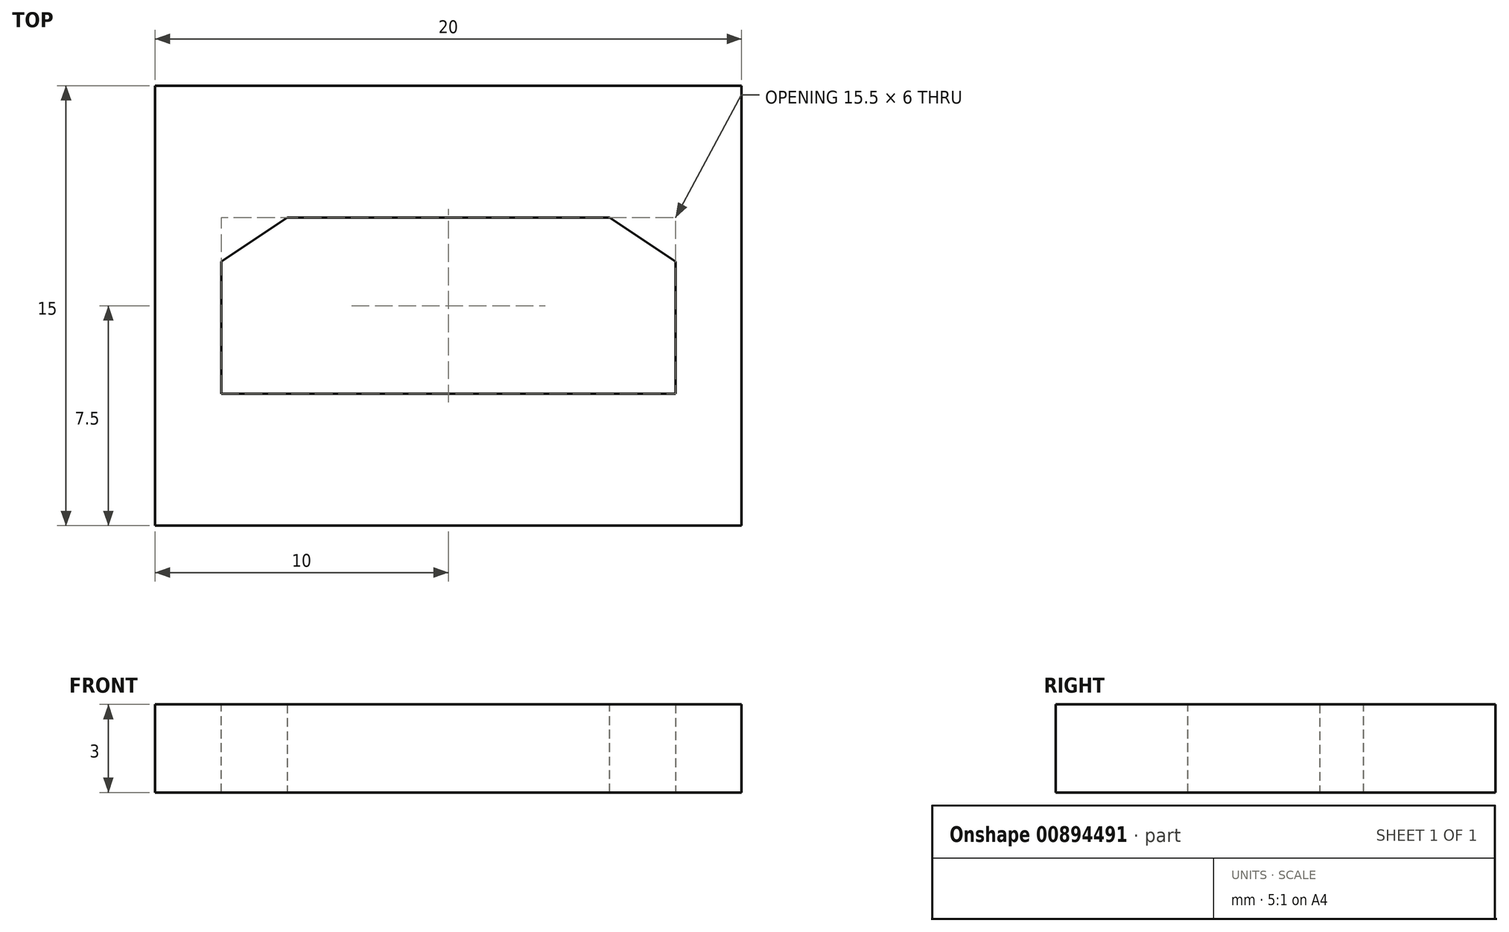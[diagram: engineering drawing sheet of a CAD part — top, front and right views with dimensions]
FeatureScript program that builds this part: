
annotation { "Feature Type Name" : "Feature", "Feature Type Description" : "" }
export const myFeature = defineFeature(function(context is Context, id is Id, definition is map)
    precondition{}
    {
        {
            var Q0;
            Q0=qCreatedBy(makeId("Top.planeOp"),FACE);
            var sketch = newSketch(context, id + "F0", { "sketchPlane" : qUnion([Q0])});
            skLineSegment(sketch, "E0.bottom", {"start": v(10, 7.5) * mm, "end": v(-10, 7.5) * mm});
            skLineSegment(sketch, "E0.top", {"start": v(10, -7.5) * mm, "end": v(-10, -7.5) * mm});
            skLineSegment(sketch, "E0.left", {"start": v(10, 7.5) * mm, "end": v(10, -7.5) * mm});
            skLineSegment(sketch, "E0.right", {"start": v(-10, 7.5) * mm, "end": v(-10, -7.5) * mm});
            skPoint(sketch, "E0.middle", {"position": v(0, 0) * mm});
            skSolve(sketch);
        }
        {
            var Q0;
            Q0=makeQuery(id+"F0.imprint","IMPRINT",FACE,{"disambiguationData":[TD([[makeQuery(id+"F0.imprint","IMPRINT",EDGE,{"derivedFrom":sQuery(id+"F0.wireOp",EDGE,"E0.bottom")}),1.0]])]});
            extrude(context, id + "F1", {"entities" : qUnion([Q0]), "depth" : 3 * mm, "offsetDistance" : 25 * mm});
        }
        {
            var Q0;
            Q0=makeQuery(id+"F1.opExtrude","CAP_FACE",FACE,{"disambiguationData":[OSD([sQuery(id+"F0.wireOp",EDGE,"E0.bottom"),sQuery(id+"F0.wireOp",EDGE,"E0.top"),sQuery(id+"F0.wireOp",EDGE,"E0.left"),sQuery(id+"F0.wireOp",EDGE,"E0.right")])],"isStart":false});
            var sketch = newSketch(context, id + "F2", { "sketchPlane" : qUnion([Q0])});
            skLineSegment(sketch, "E1.bottom", {"start": v(7.75, 3) * mm, "end": v(-7.75, 3) * mm});
            skLineSegment(sketch, "E1.top", {"start": v(7.75, -3) * mm, "end": v(-7.75, -3) * mm});
            skLineSegment(sketch, "E1.left", {"start": v(7.75, 3) * mm, "end": v(7.75, -3) * mm});
            skLineSegment(sketch, "E1.right", {"start": v(-7.75, 3) * mm, "end": v(-7.75, -3) * mm});
            skPoint(sketch, "E1.middle", {"position": v(0, 0) * mm});
            skSolve(sketch);
        }
        {
            var Q0;
            Q0=makeQuery(id+"F2.imprint","IMPRINT",FACE,{"disambiguationData":[TD([[makeQuery(id+"F2.imprint","IMPRINT",EDGE,{"derivedFrom":sQuery(id+"F2.wireOp",EDGE,"E1.bottom")}),1.0]])]});
            extrude(context, id + "F3", {"entities" : qUnion([Q0]), "operationType" : NewBodyOperationType.REMOVE, "oppositeDirection" : true, "depth" : 25 * mm, "offsetDistance" : 25 * mm});
        }
        {
            var Q0;
            Q0=makeQuery(id+"F3.boolean.opBoolean","COPY",EDGE,{"derivedFrom":makeQuery(id+"F3.opExtrude","SWEPT_EDGE",EDGE,{"disambiguationData":[OSD([sQuery(id+"F2.wireOp",EDGE,"E1.bottom"),sQuery(id+"F2.wireOp",EDGE,"E1.right")])]})});
            var Q1;
            Q1=makeQuery(id+"F3.boolean.opBoolean","COPY",EDGE,{"derivedFrom":makeQuery(id+"F3.opExtrude","SWEPT_EDGE",EDGE,{"disambiguationData":[OSD([sQuery(id+"F2.wireOp",EDGE,"E1.bottom"),sQuery(id+"F2.wireOp",EDGE,"E1.left")])]})});
            chamfer(context, id + "F4", {"entities" : qUnion([Q0, Q1]), "chamferType" : ChamferType.TWO_OFFSETS, "width1" : 1.5 * mm, "oppositeDirection" : false, "width2" : 2.25 * mm, "tangentPropagation" : true});
        }
    });
